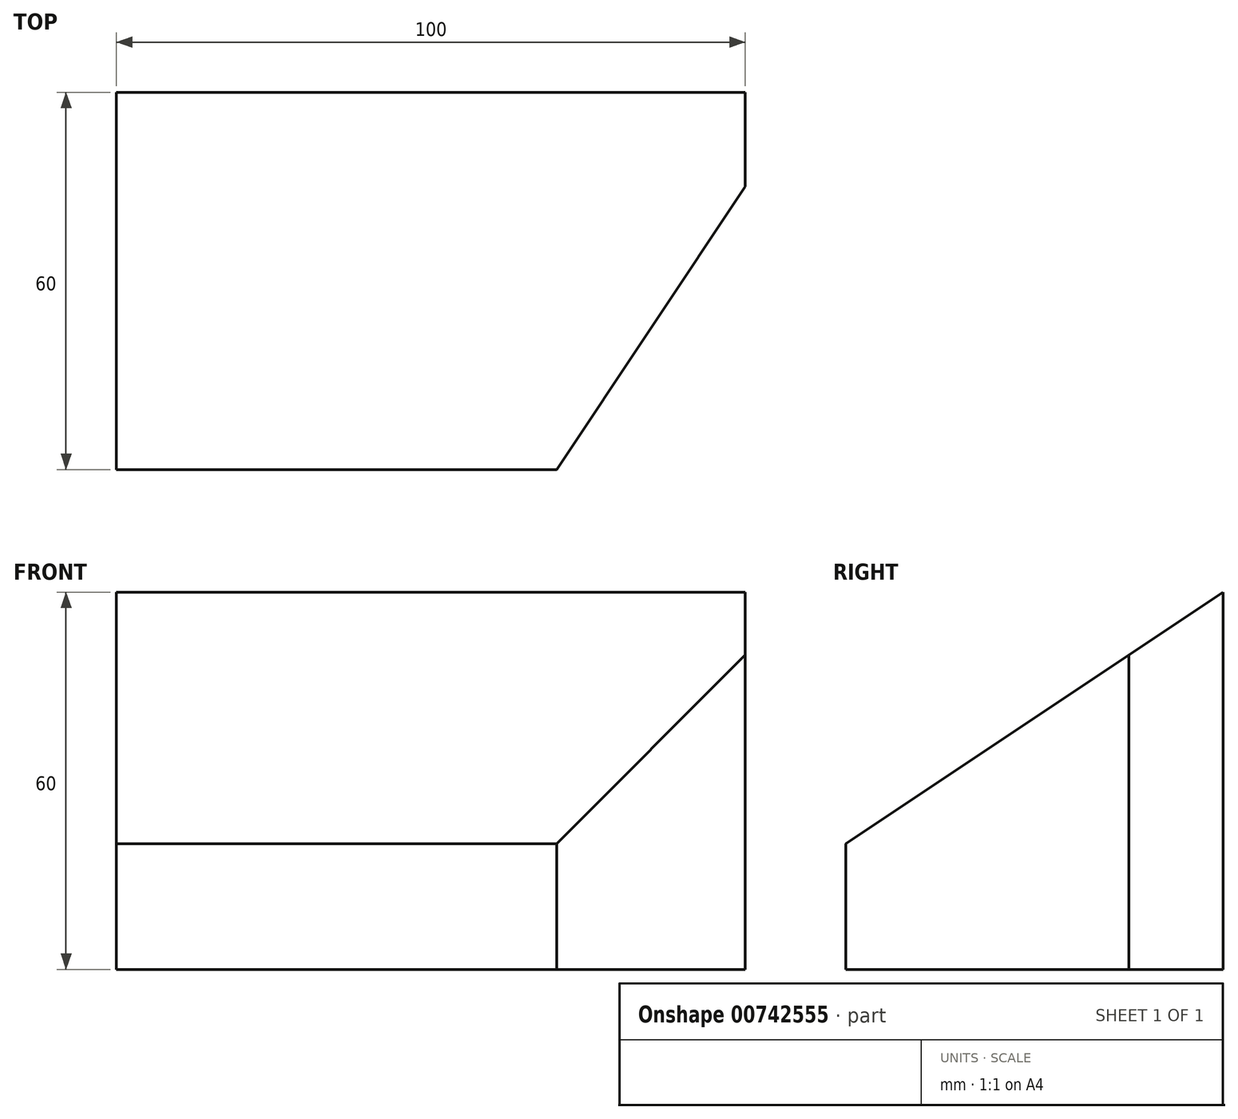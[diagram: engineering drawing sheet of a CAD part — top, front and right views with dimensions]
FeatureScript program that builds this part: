
annotation { "Feature Type Name" : "Feature", "Feature Type Description" : "" }
export const myFeature = defineFeature(function(context is Context, id is Id, definition is map)
    precondition{}
    {
        {
            var Q0;
            Q0=qCreatedBy(makeId("Top.planeOp"),FACE);
            var sketch = newSketch(context, id + "F0", { "sketchPlane" : qUnion([Q0])});
            skLineSegment(sketch, "E0", {"start": v(0, 0) * mm, "end": v(0, 60) * mm});
            skLineSegment(sketch, "E1", {"start": v(0, 60) * mm, "end": v(100, 60) * mm});
            skLineSegment(sketch, "E2", {"start": v(100, 60) * mm, "end": v(100, 45) * mm});
            skLineSegment(sketch, "E3", {"start": v(0, 0) * mm, "end": v(70, 0) * mm});
            skLineSegment(sketch, "E4", {"start": v(70, 0) * mm, "end": v(100, 45) * mm});
            skSolve(sketch);
        }
        {
            var Q0;
            Q0=makeQuery(id+"F0.imprint","IMPRINT",FACE,{"disambiguationData":[TD([[makeQuery(id+"F0.imprint","IMPRINT",EDGE,{"derivedFrom":sQuery(id+"F0.wireOp",EDGE,"E0")}),-1.0]])]});
            extrude(context, id + "F1", {"entities" : qUnion([Q0]), "depth" : 60 * mm, "offsetDistance" : 25 * mm});
        }
        {
            var Q0;
            Q0=makeQuery(id+"F1.opExtrude","SWEPT_FACE",FACE,{"disambiguationData":[OSD([sQuery(id+"F0.wireOp",EDGE,"E0")])]});
            var sketch = newSketch(context, id + "F2", { "sketchPlane" : qUnion([Q0])});
            skLineSegment(sketch, "E5", {"start": v(0, 0) * mm, "end": v(0, 20) * mm});
            skLineSegment(sketch, "E6", {"start": v(-60, 60) * mm, "end": v(0, 20) * mm});
            skLineSegment(sketch, "E7", {"start": v(0, 60) * mm, "end": v(0, 20) * mm});
            skLineSegment(sketch, "E8", {"start": v(0, 60) * mm, "end": v(-60, 60) * mm});
            skSolve(sketch);
        }
        {
            var Q0;
            Q0=makeQuery(id+"F2.imprint","IMPRINT",FACE,{"disambiguationData":[TD([[makeQuery(id+"F2.imprint","IMPRINT",EDGE,{"derivedFrom":sQuery(id+"F2.wireOp",EDGE,"E6")}),1.0]])]});
            extrude(context, id + "F3", {"entities" : qUnion([Q0]), "operationType" : NewBodyOperationType.REMOVE, "oppositeDirection" : true, "depth" : 126 * mm, "offsetDistance" : 25 * mm});
        }
    });
